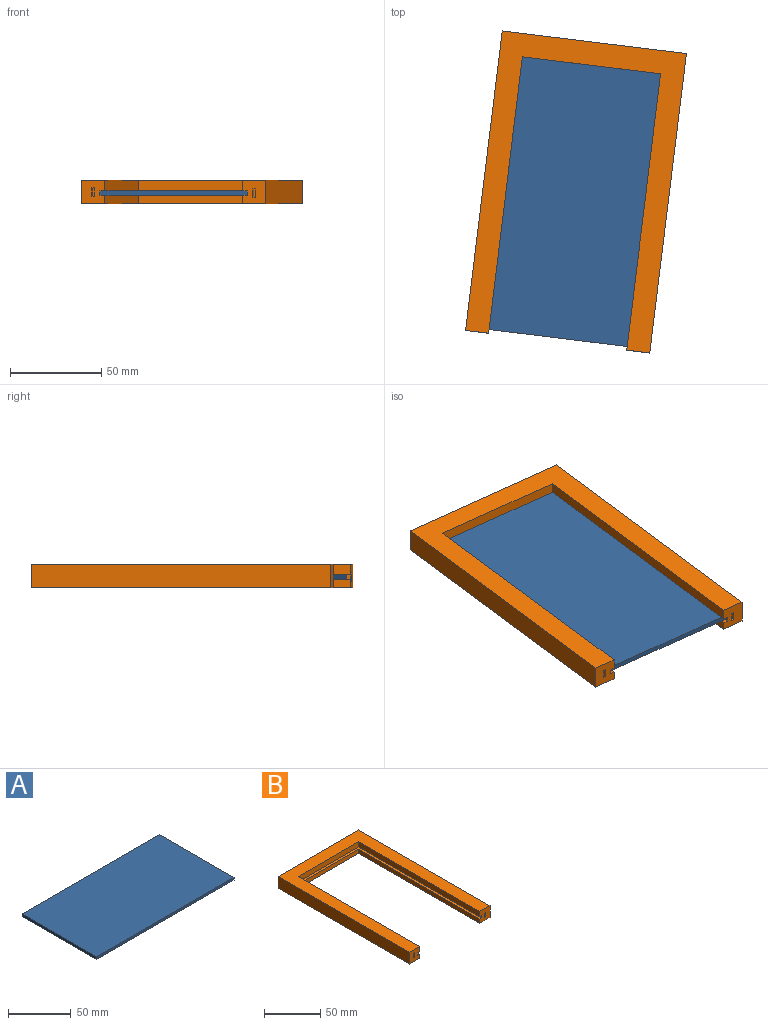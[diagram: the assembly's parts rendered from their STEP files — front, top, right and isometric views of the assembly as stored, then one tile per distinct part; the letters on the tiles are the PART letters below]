
ASSEMBLY  parts=2 mates=1
PART A: 6 faces, bbox 154.9x83.8x2.5 mm
  f0: plane 154.94x2.54mm, normal (0,1,0), area 393.5mm2, adj f1,f3,f4,f5
  f1: plane 83.82x2.54mm, normal (-1,0,0), area 212.9mm2, adj f0,f2,f4,f5
  f2: plane 154.94x2.54mm, normal (0,-1,0), area 393.5mm2, adj f1,f3,f4,f5
  f3: plane 83.82x2.54mm, normal (1,0,0), area 212.9mm2, adj f0,f2,f4,f5
  f4: plane 154.94x83.82mm, normal (0,0,1), area 12987.1mm2, adj f0,f1,f2,f3
  f5: plane 154.94x83.82mm, normal (0,0,-1), area 12987.1mm2, adj f0,f1,f2,f3
PART B: 28 faces, bbox 101.6x165.1x12.7 mm
  f0: plane 12.7x12.7mm, normal (0,-1,0), area 147.9mm2, adj f5,f6,f8,f9,f10,f11,f12,f16
  f1: plane 12.7x12.7mm, normal (0,-1,0), area 147.9mm2, adj f2,f3,f4,f5,f6,f7,f11,f12
  f2: plane 152.4x4.45mm, normal (-1,0,0), area 677.4mm2, adj f1,f5,f12,f13
  f3: plane 165.1x12.7mm, normal (1,0,0), area 2096.8mm2, adj f1,f11,f12,f14
  f4: plane 152.4x5.72mm, normal (-1,0,0), area 871mm2, adj f1,f6,f11,f15
  f5: plane 158.75x81.28mm, normal (0,0,1), area 1290.3mm2, adj f0,f1,f2,f7,f8,f13,f16,f17
  f6: plane 158.75x81.28mm, normal (0,0,-1), area 1290.3mm2, adj f0,f1,f4,f7,f10,f15,f16,f17
  f7: plane 158.75x2.54mm, normal (-1,0,0), area 403.2mm2, adj f1,f5,f6,f17
  f8: plane 152.4x4.45mm, normal (1,0,0), area 677.4mm2, adj f0,f5,f12,f13
  f9: plane 165.1x12.7mm, normal (-1,0,0), area 2096.8mm2, adj f0,f11,f12,f14
  f10: plane 152.4x5.72mm, normal (1,0,0), area 871mm2, adj f0,f6,f11,f15
  f11: plane 165.1x101.6mm, normal (0,0,1), area 5161.3mm2, adj f0,f1,f3,f4,f9,f10,f14,f15
  f12: plane 165.1x101.6mm, normal (0,0,-1), area 5161.3mm2, adj f0,f1,f2,f3,f8,f9,f13,f14
  f13: plane 76.2x4.45mm, normal (0,-1,0), area 338.7mm2, adj f2,f5,f8,f12
  f14: plane 101.6x12.7mm, normal (0,1,0), area 1290.3mm2, adj f3,f9,f11,f12
  f15: plane 76.2x5.72mm, normal (0,-1,0), area 435.5mm2, adj f4,f6,f10,f11
  f16: plane 158.75x2.54mm, normal (1,0,0), area 403.2mm2, adj f0,f5,f6,f17
  f17: plane 81.28x2.54mm, normal (0,-1,0), area 206.5mm2, adj f5,f6,f7,f16
  f18: plane 3.81x1.52mm, normal (0,0,1), area 5.8mm2, adj f1,f19,f21,f22
  f19: plane 4.57x3.81mm, normal (-1,0,0), area 17.4mm2, adj f1,f18,f20,f22
  f20: plane 3.81x1.52mm, normal (0,0,-1), area 5.8mm2, adj f1,f19,f21,f22
  f21: plane 4.57x3.81mm, normal (1,0,0), area 17.4mm2, adj f1,f18,f20,f22
  f22: plane 4.57x1.52mm, normal (0,-1,0), area 7mm2, adj f18,f19,f20,f21
  f23: plane 4.57x3.81mm, normal (1,0,0), area 17.4mm2, adj f0,f24,f26,f27
  f24: plane 3.81x1.52mm, normal (0,0,1), area 5.8mm2, adj f0,f23,f25,f27
  f25: plane 4.57x3.81mm, normal (-1,0,0), area 17.4mm2, adj f0,f24,f26,f27
  f26: plane 3.81x1.52mm, normal (0,0,-1), area 5.8mm2, adj f0,f23,f25,f27
  f27: plane 4.57x1.52mm, normal (0,-1,0), area 7mm2, adj f23,f24,f25,f26
PLACE A rot(axis=(0,0,-1),97deg) t=(47.76,-132.77,-47.98)mm
PLACE B rot(axis=(0,0,-1),7deg) t=(-45.83,-125.91,-52.44)mm
MATE parallel B.f7 <-> A.f0  axis (-0.99,0.12,0) through (36.06,-209.51,-46.73)mm
